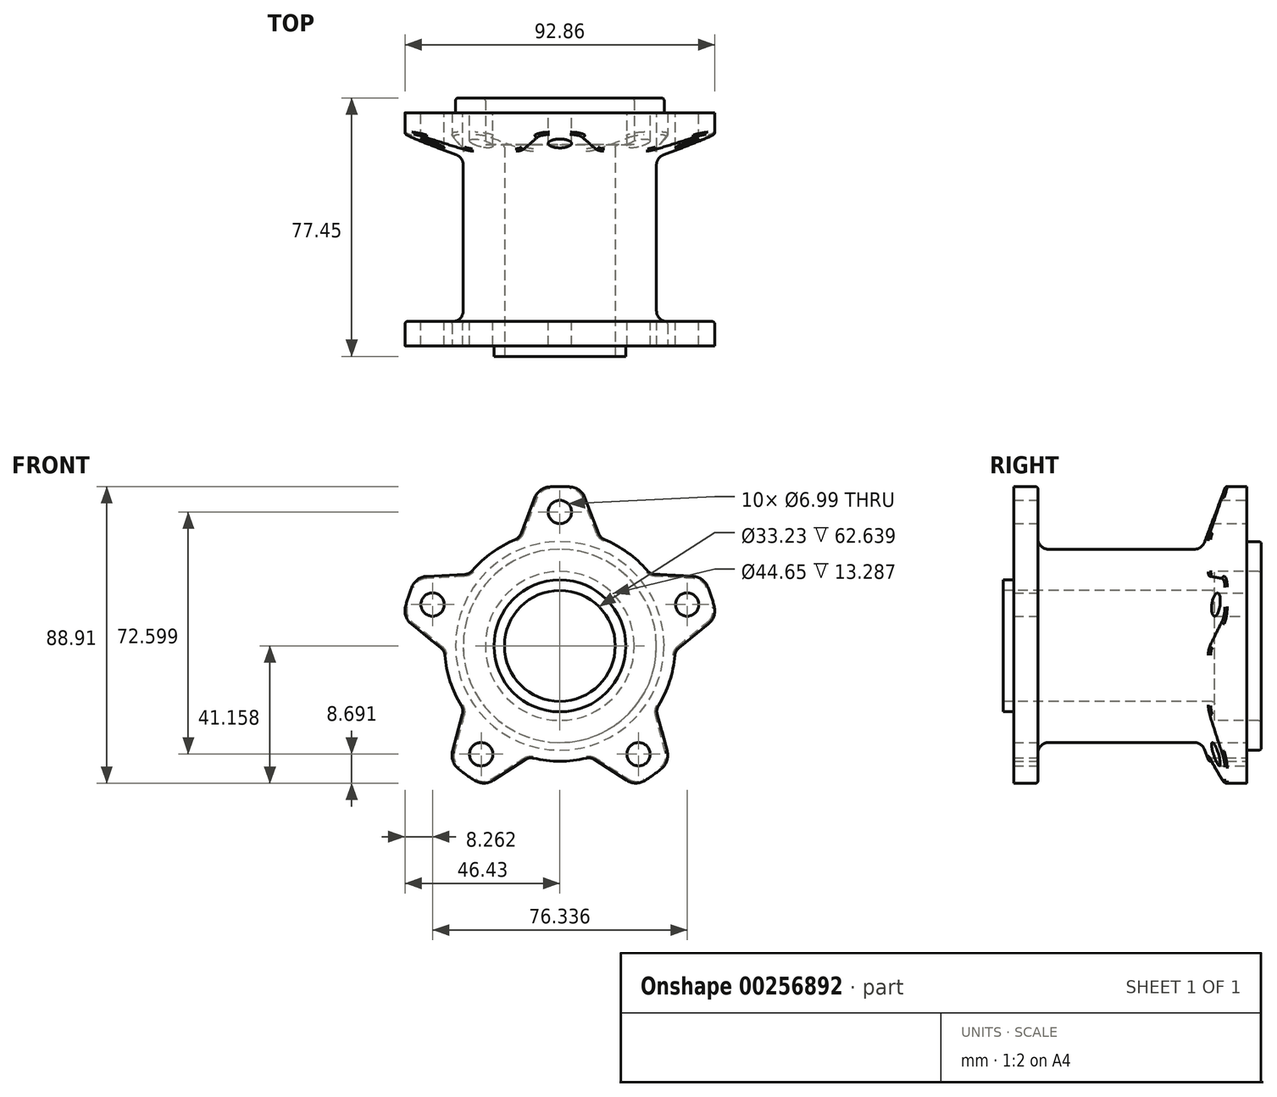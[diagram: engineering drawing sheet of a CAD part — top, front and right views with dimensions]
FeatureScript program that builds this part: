
annotation { "Feature Type Name" : "Feature", "Feature Type Description" : "" }
export const myFeature = defineFeature(function(context is Context, id is Id, definition is map)
    precondition{}
    {
        {
            var Q0;
            Q0=qCreatedBy(makeId("Right.planeOp"),FACE);
            var sketch = newSketch(context, id + "F0", { "sketchPlane" : qUnion([Q0])});
            skLineSegment(sketch, "E0", {"start": v(0, 0) * mm, "end": v(7.28, 0) * mm});
            skLineSegment(sketch, "E1", {"start": v(-3.18, -28) * mm, "end": v(0, -28) * mm});
            skLineSegment(sketch, "E2", {"start": v(0, -28) * mm, "end": v(0, 0) * mm});
            skLineSegment(sketch, "E3", {"start": v(69.85, 0) * mm, "end": v(69.85, -16.5) * mm});
            skLineSegment(sketch, "E4", {"start": v(-3.17, -47.75) * mm, "end": v(76.5, -47.75) * mm});
            skLineSegment(sketch, "E5", {"start": v(-3.18, -31.13) * mm, "end": v(-3.18, -28) * mm});
            skLineSegment(sketch, "E6", {"start": v(7.28, 0) * mm, "end": v(7.28, -18.79) * mm});
            skLineSegment(sketch, "E7", {"start": v(7.28, -18.79) * mm, "end": v(56.42, -18.79) * mm});
            skLineSegment(sketch, "E8", {"start": v(56.42, -18.79) * mm, "end": v(63.51, 0) * mm});
            skLineSegment(sketch, "E9.trimOffspring", {"start": v(63.51, 0) * mm, "end": v(69.85, 0) * mm});
            skLineSegment(sketch, "E10", {"start": v(-3.18, -31.13) * mm, "end": v(60.23, -31.13) * mm});
            skLineSegment(sketch, "E11", {"start": v(60.23, -31.13) * mm, "end": v(60.23, -25.43) * mm});
            skLineSegment(sketch, "E12", {"start": v(60.23, -25.43) * mm, "end": v(74.27, -25.43) * mm});
            skLineSegment(sketch, "E13", {"start": v(74.27, -25.43) * mm, "end": v(74.27, -16.5) * mm});
            skLineSegment(sketch, "E14", {"start": v(74.27, -16.5) * mm, "end": v(69.85, -16.5) * mm});
            skSolve(sketch);
        }
        {
            var Q0;
            Q0 = qSketchRegion(id + "F0", true);
            var Q1;
            Q1=sQuery(id+"F0.wireOp",EDGE,"E4");
            revolve(context, id + "F1", {"entities" : qUnion([Q0]), "axis" : qUnion([Q1]), "revolveType" : RevolveType.FULL});
        }
        {
            var Q0;
            Q0=makeQuery(id+"F1.opRevolve","SWEPT_FACE",FACE,{"disambiguationData":[OSD([sQuery(id+"F0.wireOp",EDGE,"E3")])]});
            var sketch = newSketch(context, id + "F2", { "sketchPlane" : qUnion([Q0])});
            skCircle(sketch, "E15", {"center": v(0, -7.62) * mm, "radius": 3.5 * mm});
            skCircle(sketch, "E16.1.0", {"center": v(-38.17, -35.35) * mm, "radius": 3.5 * mm});
            skCircle(sketch, "E16.2.0", {"center": v(-23.59, -80.22) * mm, "radius": 3.5 * mm});
            skCircle(sketch, "E16.3.0", {"center": v(23.59, -80.22) * mm, "radius": 3.5 * mm});
            skCircle(sketch, "E16.4.0", {"center": v(38.17, -35.35) * mm, "radius": 3.5 * mm});
            skPoint(sketch, "E16.center", {"position": v(0, -47.75) * mm});
            skSolve(sketch);
        }
        {
            var Q0;
            Q0 = qSketchRegion(id + "F2", true);
            extrude(context, id + "F3", {"entities" : qUnion([Q0]), "operationType" : NewBodyOperationType.REMOVE, "endBound" : BoundingType.THROUGH_ALL, "oppositeDirection" : true, "depth" : 25.4 * mm});
        }
        {
            var Q0;
            Q0=makeQuery(id+"F1.opRevolve","SWEPT_FACE",FACE,{"disambiguationData":[OSD([sQuery(id+"F0.wireOp",EDGE,"E3")])]});
            var sketch = newSketch(context, id + "F4", { "sketchPlane" : qUnion([Q0])});
            skLineSegment(sketch, "E17", {"start": v(-6.22, 0) * mm, "end": v(-11.62, -14.07) * mm});
            skLineSegment(sketch, "E18.MirrorCS", {"start": v(6.22, 0) * mm, "end": v(11.62, -14.07) * mm});
            skLineSegment(sketch, "E19.1.1", {"start": v(-43.5, -27.08) * mm, "end": v(-28.44, -26.3) * mm});
            skLineSegment(sketch, "E19.1.3", {"start": v(-47.34, -38.92) * mm, "end": v(-35.62, -48.4) * mm});
            skLineSegment(sketch, "E19.2.1", {"start": v(-33.1, -82.73) * mm, "end": v(-29.2, -68.17) * mm});
            skLineSegment(sketch, "E19.2.3", {"start": v(-23.03, -90.04) * mm, "end": v(-10.4, -81.83) * mm});
            skLineSegment(sketch, "E19.3.1", {"start": v(23.03, -90.04) * mm, "end": v(10.4, -81.83) * mm});
            skLineSegment(sketch, "E19.3.3", {"start": v(33.1, -82.73) * mm, "end": v(29.2, -68.17) * mm});
            skLineSegment(sketch, "E19.4.1", {"start": v(47.34, -38.92) * mm, "end": v(35.62, -48.4) * mm});
            skLineSegment(sketch, "E19.4.3", {"start": v(43.5, -27.08) * mm, "end": v(28.44, -26.3) * mm});
            skPoint(sketch, "E19.center", {"position": v(0, -47.75) * mm});
            skArc(sketch, "E20", {"start": v(-13.36, -15.86) * mm, "mid": v(-20.32, -19.78) * mm, "end": v(-26.2, -25.2) * mm});
            skArc(sketch, "E21", {"start": v(26.2, -25.2) * mm, "mid": v(20.32, -19.78) * mm, "end": v(13.36, -15.86) * mm});
            skArc(sketch, "E22", {"start": v(29.55, -65.7) * mm, "mid": v(32.88, -58.44) * mm, "end": v(34.45, -50.6) * mm});
            skArc(sketch, "E23", {"start": v(-7.94, -81.4) * mm, "mid": v(0, -82.32) * mm, "end": v(7.94, -81.4) * mm});
            skArc(sketch, "E24", {"start": v(-29.55, -65.7) * mm, "mid": v(-32.88, -58.44) * mm, "end": v(-34.45, -50.6) * mm});
            skArc(sketch, "E25", {"start": v(-47.34, -38.92) * mm, "mid": v(-45.8, -62.63) * mm, "end": v(-33.1, -82.73) * mm});
            skArc(sketch, "E26.trimOffspring", {"start": v(-23.03, -90.04) * mm, "mid": v(0, -95.9) * mm, "end": v(23.03, -90.04) * mm});
            skArc(sketch, "E27.trimOffspring", {"start": v(33.1, -82.73) * mm, "mid": v(45.8, -62.63) * mm, "end": v(47.34, -38.92) * mm});
            skArc(sketch, "E28.trimOffspring", {"start": v(43.5, -27.08) * mm, "mid": v(28.3, -8.8) * mm, "end": v(6.22, 0) * mm});
            skArc(sketch, "E29.trimOffspring", {"start": v(-6.22, 0) * mm, "mid": v(-28.3, -8.8) * mm, "end": v(-43.5, -27.08) * mm});
            skPoint(sketch, "E30.end.orphan", {"position": v(0, -15.37) * mm});
            skPoint(sketch, "E31.visualSharp", {"position": v(-27.05, -26.22) * mm});
            skArc(sketch, "E31.filletArc", {"start": v(-28.44, -26.3) * mm, "mid": v(-27.2, -25.97) * mm, "end": v(-26.2, -25.2) * mm});
            skPoint(sketch, "E32.visualSharp", {"position": v(-12.12, -15.37) * mm});
            skArc(sketch, "E32.filletArc", {"start": v(-13.36, -15.86) * mm, "mid": v(-12.3, -15.15) * mm, "end": v(-11.62, -14.07) * mm});
            skPoint(sketch, "E33.visualSharp", {"position": v(12.12, -15.37) * mm});
            skArc(sketch, "E33.filletArc", {"start": v(11.62, -14.07) * mm, "mid": v(12.3, -15.15) * mm, "end": v(13.36, -15.86) * mm});
            skPoint(sketch, "E34.visualSharp", {"position": v(27.05, -26.22) * mm});
            skArc(sketch, "E34.filletArc", {"start": v(26.2, -25.2) * mm, "mid": v(27.2, -25.97) * mm, "end": v(28.44, -26.3) * mm});
            skPoint(sketch, "E35.visualSharp", {"position": v(34.54, -49.27) * mm});
            skArc(sketch, "E35.filletArc", {"start": v(35.62, -48.4) * mm, "mid": v(34.81, -49.38) * mm, "end": v(34.45, -50.6) * mm});
            skPoint(sketch, "E36.visualSharp", {"position": v(28.84, -66.82) * mm});
            skArc(sketch, "E36.filletArc", {"start": v(29.55, -65.7) * mm, "mid": v(29.12, -66.9) * mm, "end": v(29.2, -68.17) * mm});
            skPoint(sketch, "E37.visualSharp", {"position": v(9.23, -81.07) * mm});
            skArc(sketch, "E37.filletArc", {"start": v(10.4, -81.83) * mm, "mid": v(9.2, -81.36) * mm, "end": v(7.94, -81.4) * mm});
            skPoint(sketch, "E38.visualSharp", {"position": v(-9.23, -81.07) * mm});
            skArc(sketch, "E38.filletArc", {"start": v(-7.94, -81.4) * mm, "mid": v(-9.2, -81.36) * mm, "end": v(-10.4, -81.83) * mm});
            skPoint(sketch, "E39.visualSharp", {"position": v(-28.84, -66.82) * mm});
            skArc(sketch, "E39.filletArc", {"start": v(-29.2, -68.17) * mm, "mid": v(-29.12, -66.9) * mm, "end": v(-29.55, -65.7) * mm});
            skPoint(sketch, "E40.visualSharp", {"position": v(-34.54, -49.27) * mm});
            skArc(sketch, "E40.filletArc", {"start": v(-34.45, -50.6) * mm, "mid": v(-34.81, -49.38) * mm, "end": v(-35.62, -48.4) * mm});
            skSolve(sketch);
        }
        {
            var Q0;
            Q0 = qSketchRegion(id + "F4", true);
            extrude(context, id + "F5", {"entities" : qUnion([Q0]), "operationType" : NewBodyOperationType.REMOVE, "endBound" : BoundingType.THROUGH_ALL, "oppositeDirection" : true, "depth" : 25.4 * mm});
        }
        {
            var Q0;
            Q0=makeQuery(id+"F5.boolean.opBoolean","INTERSECT",EDGE,{"derivedFrom":[makeQuery(id+"F1.opRevolve","SWEPT_FACE",FACE,{"disambiguationData":[OSD([sQuery(id+"F0.wireOp",EDGE,"E9.trimOffspring")])]}),makeQuery(id+"F5.opExtrude","SWEPT_FACE",FACE,{"disambiguationData":[OSD([sQuery(id+"F4.wireOp",EDGE,"E17")])]})]});
            var Q1;
            Q1=makeQuery(id+"F5.boolean.opBoolean","INTERSECT",EDGE,{"derivedFrom":[makeQuery(id+"F1.opRevolve","SWEPT_FACE",FACE,{"disambiguationData":[OSD([sQuery(id+"F0.wireOp",EDGE,"E9.trimOffspring")])]}),makeQuery(id+"F5.opExtrude","SWEPT_FACE",FACE,{"disambiguationData":[OSD([sQuery(id+"F4.wireOp",EDGE,"E18.MirrorCS")])]})]});
            var Q2;
            Q2=makeQuery(id+"F5.boolean.opBoolean","INTERSECT",EDGE,{"derivedFrom":[makeQuery(id+"F1.opRevolve","SWEPT_FACE",FACE,{"disambiguationData":[OSD([sQuery(id+"F0.wireOp",EDGE,"E9.trimOffspring")])]}),makeQuery(id+"F5.opExtrude","SWEPT_FACE",FACE,{"disambiguationData":[OSD([sQuery(id+"F4.wireOp",EDGE,"E19.4.3")])]})]});
            var Q3;
            Q3=makeQuery(id+"F5.boolean.opBoolean","INTERSECT",EDGE,{"derivedFrom":[makeQuery(id+"F1.opRevolve","SWEPT_FACE",FACE,{"disambiguationData":[OSD([sQuery(id+"F0.wireOp",EDGE,"E9.trimOffspring")])]}),makeQuery(id+"F5.opExtrude","SWEPT_FACE",FACE,{"disambiguationData":[OSD([sQuery(id+"F4.wireOp",EDGE,"E19.4.1")])]})]});
            var Q4;
            Q4=makeQuery(id+"F5.boolean.opBoolean","INTERSECT",EDGE,{"derivedFrom":[makeQuery(id+"F1.opRevolve","SWEPT_FACE",FACE,{"disambiguationData":[OSD([sQuery(id+"F0.wireOp",EDGE,"E9.trimOffspring")])]}),makeQuery(id+"F5.opExtrude","SWEPT_FACE",FACE,{"disambiguationData":[OSD([sQuery(id+"F4.wireOp",EDGE,"E19.3.3")])]})]});
            var Q5;
            Q5=makeQuery(id+"F5.boolean.opBoolean","INTERSECT",EDGE,{"derivedFrom":[makeQuery(id+"F1.opRevolve","SWEPT_FACE",FACE,{"disambiguationData":[OSD([sQuery(id+"F0.wireOp",EDGE,"E9.trimOffspring")])]}),makeQuery(id+"F5.opExtrude","SWEPT_FACE",FACE,{"disambiguationData":[OSD([sQuery(id+"F4.wireOp",EDGE,"E19.3.1")])]})]});
            var Q6;
            Q6=makeQuery(id+"F5.boolean.opBoolean","INTERSECT",EDGE,{"derivedFrom":[makeQuery(id+"F1.opRevolve","SWEPT_FACE",FACE,{"disambiguationData":[OSD([sQuery(id+"F0.wireOp",EDGE,"E9.trimOffspring")])]}),makeQuery(id+"F5.opExtrude","SWEPT_FACE",FACE,{"disambiguationData":[OSD([sQuery(id+"F4.wireOp",EDGE,"E19.2.3")])]})]});
            var Q7;
            Q7=makeQuery(id+"F5.boolean.opBoolean","INTERSECT",EDGE,{"derivedFrom":[makeQuery(id+"F1.opRevolve","SWEPT_FACE",FACE,{"disambiguationData":[OSD([sQuery(id+"F0.wireOp",EDGE,"E9.trimOffspring")])]}),makeQuery(id+"F5.opExtrude","SWEPT_FACE",FACE,{"disambiguationData":[OSD([sQuery(id+"F4.wireOp",EDGE,"E19.2.1")])]})]});
            var Q8;
            Q8=makeQuery(id+"F5.boolean.opBoolean","INTERSECT",EDGE,{"derivedFrom":[makeQuery(id+"F1.opRevolve","SWEPT_FACE",FACE,{"disambiguationData":[OSD([sQuery(id+"F0.wireOp",EDGE,"E9.trimOffspring")])]}),makeQuery(id+"F5.opExtrude","SWEPT_FACE",FACE,{"disambiguationData":[OSD([sQuery(id+"F4.wireOp",EDGE,"E19.1.3")])]})]});
            var Q9;
            Q9=makeQuery(id+"F5.boolean.opBoolean","INTERSECT",EDGE,{"derivedFrom":[makeQuery(id+"F1.opRevolve","SWEPT_FACE",FACE,{"disambiguationData":[OSD([sQuery(id+"F0.wireOp",EDGE,"E9.trimOffspring")])]}),makeQuery(id+"F5.opExtrude","SWEPT_FACE",FACE,{"disambiguationData":[OSD([sQuery(id+"F4.wireOp",EDGE,"E19.1.1")])]})]});
            var Q10;
            Q10=makeQuery(id+"F5.boolean.opBoolean","INTERSECT",EDGE,{"derivedFrom":[makeQuery(id+"F1.opRevolve","SWEPT_FACE",FACE,{"disambiguationData":[OSD([sQuery(id+"F0.wireOp",EDGE,"E0")])]}),makeQuery(id+"F5.opExtrude","SWEPT_FACE",FACE,{"disambiguationData":[OSD([sQuery(id+"F4.wireOp",EDGE,"E19.2.1")])]})]});
            var Q11;
            Q11=makeQuery(id+"F5.boolean.opBoolean","INTERSECT",EDGE,{"derivedFrom":[makeQuery(id+"F1.opRevolve","SWEPT_FACE",FACE,{"disambiguationData":[OSD([sQuery(id+"F0.wireOp",EDGE,"E0")])]}),makeQuery(id+"F5.opExtrude","SWEPT_FACE",FACE,{"disambiguationData":[OSD([sQuery(id+"F4.wireOp",EDGE,"E19.2.3")])]})]});
            var Q12;
            Q12=makeQuery(id+"F5.boolean.opBoolean","INTERSECT",EDGE,{"derivedFrom":[makeQuery(id+"F1.opRevolve","SWEPT_FACE",FACE,{"disambiguationData":[OSD([sQuery(id+"F0.wireOp",EDGE,"E0")])]}),makeQuery(id+"F5.opExtrude","SWEPT_FACE",FACE,{"disambiguationData":[OSD([sQuery(id+"F4.wireOp",EDGE,"E19.1.3")])]})]});
            var Q13;
            Q13=makeQuery(id+"F5.boolean.opBoolean","INTERSECT",EDGE,{"derivedFrom":[makeQuery(id+"F1.opRevolve","SWEPT_FACE",FACE,{"disambiguationData":[OSD([sQuery(id+"F0.wireOp",EDGE,"E0")])]}),makeQuery(id+"F5.opExtrude","SWEPT_FACE",FACE,{"disambiguationData":[OSD([sQuery(id+"F4.wireOp",EDGE,"E19.1.1")])]})]});
            var Q14;
            Q14=makeQuery(id+"F5.boolean.opBoolean","INTERSECT",EDGE,{"derivedFrom":[makeQuery(id+"F1.opRevolve","SWEPT_FACE",FACE,{"disambiguationData":[OSD([sQuery(id+"F0.wireOp",EDGE,"E0")])]}),makeQuery(id+"F5.opExtrude","SWEPT_FACE",FACE,{"disambiguationData":[OSD([sQuery(id+"F4.wireOp",EDGE,"E17")])]})]});
            var Q15;
            Q15=makeQuery(id+"F5.boolean.opBoolean","INTERSECT",EDGE,{"derivedFrom":[makeQuery(id+"F1.opRevolve","SWEPT_FACE",FACE,{"disambiguationData":[OSD([sQuery(id+"F0.wireOp",EDGE,"E0")])]}),makeQuery(id+"F5.opExtrude","SWEPT_FACE",FACE,{"disambiguationData":[OSD([sQuery(id+"F4.wireOp",EDGE,"E18.MirrorCS")])]})]});
            var Q16;
            Q16=makeQuery(id+"F5.boolean.opBoolean","INTERSECT",EDGE,{"derivedFrom":[makeQuery(id+"F1.opRevolve","SWEPT_FACE",FACE,{"disambiguationData":[OSD([sQuery(id+"F0.wireOp",EDGE,"E0")])]}),makeQuery(id+"F5.opExtrude","SWEPT_FACE",FACE,{"disambiguationData":[OSD([sQuery(id+"F4.wireOp",EDGE,"E19.4.1")])]})]});
            var Q17;
            Q17=makeQuery(id+"F5.boolean.opBoolean","INTERSECT",EDGE,{"derivedFrom":[makeQuery(id+"F1.opRevolve","SWEPT_FACE",FACE,{"disambiguationData":[OSD([sQuery(id+"F0.wireOp",EDGE,"E0")])]}),makeQuery(id+"F5.opExtrude","SWEPT_FACE",FACE,{"disambiguationData":[OSD([sQuery(id+"F4.wireOp",EDGE,"E19.4.3")])]})]});
            var Q18;
            Q18=makeQuery(id+"F5.boolean.opBoolean","INTERSECT",EDGE,{"derivedFrom":[makeQuery(id+"F1.opRevolve","SWEPT_FACE",FACE,{"disambiguationData":[OSD([sQuery(id+"F0.wireOp",EDGE,"E0")])]}),makeQuery(id+"F5.opExtrude","SWEPT_FACE",FACE,{"disambiguationData":[OSD([sQuery(id+"F4.wireOp",EDGE,"E19.3.3")])]})]});
            var Q19;
            Q19=makeQuery(id+"F5.boolean.opBoolean","INTERSECT",EDGE,{"derivedFrom":[makeQuery(id+"F1.opRevolve","SWEPT_FACE",FACE,{"disambiguationData":[OSD([sQuery(id+"F0.wireOp",EDGE,"E0")])]}),makeQuery(id+"F5.opExtrude","SWEPT_FACE",FACE,{"disambiguationData":[OSD([sQuery(id+"F4.wireOp",EDGE,"E19.3.1")])]})]});
            fillet(context, id + "F6", {"entities" : qUnion([Q0, Q1, Q2, Q3, Q4, Q5, Q6, Q7, Q8, Q9, Q10, Q11, Q12, Q13, Q14, Q15, Q16, Q17, Q18, Q19]), "radius" : 5.08 * mm, "tangentPropagation" : true, "allowEdgeOverflow" : false});
        }
        {
            var Q0;
            Q0=makeQuery(id+"F1.opRevolve","SWEPT_EDGE",EDGE,{"disambiguationData":[OSD([sQuery(id+"F0.wireOp",EDGE,"E6"),sQuery(id+"F0.wireOp",EDGE,"E7")])]});
            var Q1;
            Q1=makeQuery(id+"F1.opRevolve","SWEPT_EDGE",EDGE,{"disambiguationData":[OSD([sQuery(id+"F0.wireOp",EDGE,"E7"),sQuery(id+"F0.wireOp",EDGE,"E8")])]});
            fillet(context, id + "F7", {"entities" : qUnion([Q0, Q1]), "radius" : 3.17 * mm, "tangentPropagation" : true, "allowEdgeOverflow" : false});
        }
        {
            var Q0;
            Q0=makeQuery(id+"F5.boolean.opBoolean","INTERSECT",EDGE,{"derivedFrom":[makeQuery(id+"F1.opRevolve","SWEPT_FACE",FACE,{"disambiguationData":[OSD([sQuery(id+"F0.wireOp",EDGE,"E6")])]}),makeQuery(id+"F5.opExtrude","SWEPT_FACE",FACE,{"disambiguationData":[OSD([sQuery(id+"F4.wireOp",EDGE,"E17")])]})]});
            var Q1;
            Q1=makeQuery(id+"F5.boolean.opBoolean","INTERSECT",EDGE,{"derivedFrom":[makeQuery(id+"F1.opRevolve","SWEPT_FACE",FACE,{"disambiguationData":[OSD([sQuery(id+"F0.wireOp",EDGE,"E8")])]}),makeQuery(id+"F5.opExtrude","SWEPT_FACE",FACE,{"disambiguationData":[OSD([sQuery(id+"F4.wireOp",EDGE,"E17")])]})]});
            var Q2;
            Q2=makeQuery(id+"F1.opRevolve","SWEPT_EDGE",EDGE,{"disambiguationData":[OSD([sQuery(id+"F0.wireOp",EDGE,"E13"),sQuery(id+"F0.wireOp",EDGE,"E14")])]});
            var Q3;
            Q3=makeQuery(id+"F1.opRevolve","SWEPT_EDGE",EDGE,{"disambiguationData":[OSD([sQuery(id+"F0.wireOp",EDGE,"E12"),sQuery(id+"F0.wireOp",EDGE,"E13")])]});
            var Q4;
            Q4=makeQuery(id+"F1.opRevolve","SWEPT_EDGE",EDGE,{"disambiguationData":[OSD([sQuery(id+"F0.wireOp",EDGE,"E10"),sQuery(id+"F0.wireOp",EDGE,"E11")])]});
            fillet(context, id + "F8", {"entities" : qUnion([Q0, Q1, Q2, Q3, Q4]), "radius" : 0.76 * mm, "tangentPropagation" : true, "allowEdgeOverflow" : false});
        }
    });
